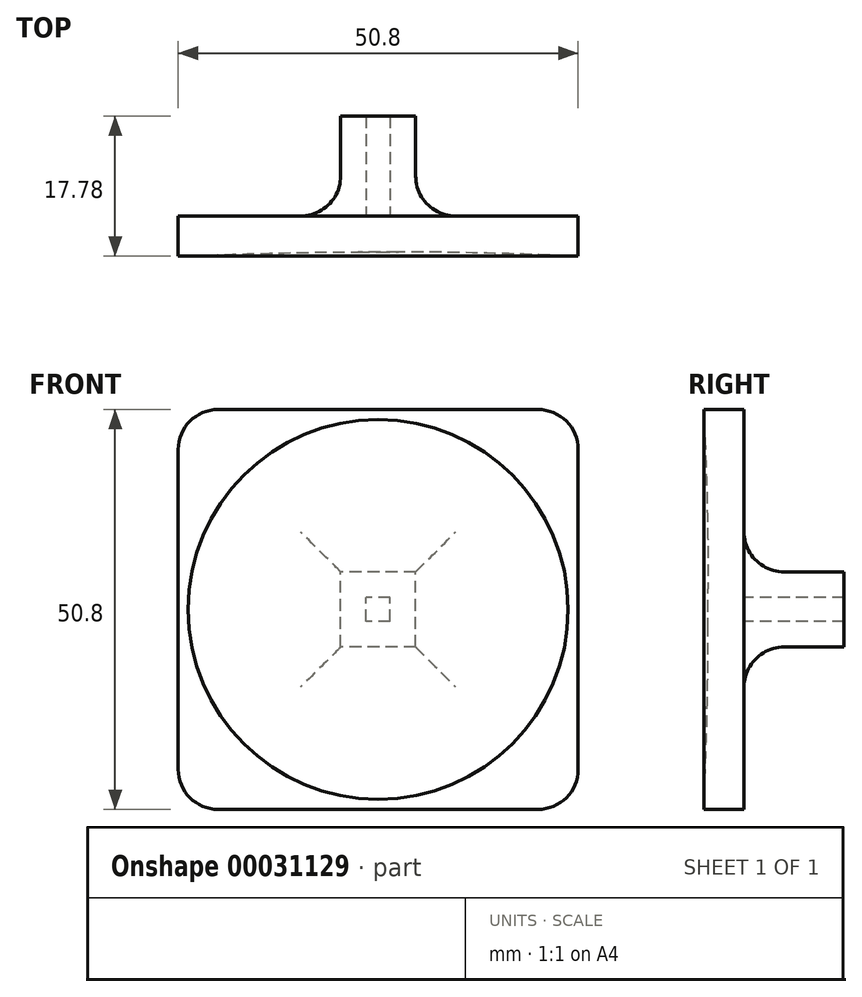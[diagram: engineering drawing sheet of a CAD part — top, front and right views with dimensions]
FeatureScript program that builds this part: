
annotation { "Feature Type Name" : "Feature", "Feature Type Description" : "" }
export const myFeature = defineFeature(function(context is Context, id is Id, definition is map)
    precondition{}
    {
        {
            var Q0;
            Q0=qCreatedBy(makeId("Front.planeOp"),FACE);
            var sketch = newSketch(context, id + "F0", { "sketchPlane" : qUnion([Q0])});
            skLineSegment(sketch, "E0.rect.bottom", {"start": v(25.4, -25.4) * mm, "end": v(-25.4, -25.4) * mm});
            skLineSegment(sketch, "E0.rect.top", {"start": v(25.4, 25.4) * mm, "end": v(-25.4, 25.4) * mm});
            skLineSegment(sketch, "E0.rect.left", {"start": v(25.4, -25.4) * mm, "end": v(25.4, 25.4) * mm});
            skLineSegment(sketch, "E0.rect.right", {"start": v(-25.4, -25.4) * mm, "end": v(-25.4, 25.4) * mm});
            skPoint(sketch, "E0.rect.middle", {"position": v(0, 0) * mm});
            skSolve(sketch);
        }
        {
            var Q0;
            Q0=makeQuery(id+"F0.imprint","IMPRINT",FACE,{"disambiguationData":[TD([[makeQuery(id+"F0.imprint","IMPRINT",EDGE,{"derivedFrom":sQuery(id+"F0.wireOp",EDGE,"E0.rect.bottom")}),-1.0]])]});
            extrude(context, id + "F1", {"entities" : qUnion([Q0]), "depth" : 5.08 * mm});
        }
        {
            var Q0;
            Q0=makeQuery(id+"F1.opExtrude","CAP_FACE",FACE,{"disambiguationData":[OSD([sQuery(id+"F0.wireOp",EDGE,"E0.rect.bottom"),sQuery(id+"F0.wireOp",EDGE,"E0.rect.top"),sQuery(id+"F0.wireOp",EDGE,"E0.rect.left"),sQuery(id+"F0.wireOp",EDGE,"E0.rect.right")])],"isStart":true});
            var sketch = newSketch(context, id + "F2", { "sketchPlane" : qUnion([Q0])});
            skLineSegment(sketch, "E1.rect.bottom", {"start": v(-4.76, -4.76) * mm, "end": v(4.76, -4.76) * mm});
            skLineSegment(sketch, "E1.rect.top", {"start": v(-4.76, 4.76) * mm, "end": v(4.76, 4.76) * mm});
            skLineSegment(sketch, "E1.rect.left", {"start": v(-4.76, -4.76) * mm, "end": v(-4.76, 4.76) * mm});
            skLineSegment(sketch, "E1.rect.right", {"start": v(4.76, -4.76) * mm, "end": v(4.76, 4.76) * mm});
            skPoint(sketch, "E1.rect.middle", {"position": v(0, 0) * mm});
            skLineSegment(sketch, "E2.rect.bottom", {"start": v(-1.52, -1.52) * mm, "end": v(1.52, -1.52) * mm});
            skLineSegment(sketch, "E2.rect.top", {"start": v(-1.52, 1.52) * mm, "end": v(1.52, 1.52) * mm});
            skLineSegment(sketch, "E2.rect.left", {"start": v(-1.52, -1.52) * mm, "end": v(-1.52, 1.52) * mm});
            skLineSegment(sketch, "E2.rect.right", {"start": v(1.52, -1.52) * mm, "end": v(1.52, 1.52) * mm});
            skSolve(sketch);
        }
        {
            var Q0;
            Q0=makeQuery(id+"F2.imprint","IMPRINT",FACE,{"disambiguationData":[TD([[makeQuery(id+"F2.imprint","IMPRINT",EDGE,{"derivedFrom":sQuery(id+"F2.wireOp",EDGE,"E1.rect.bottom")}),1.0]])]});
            extrude(context, id + "F3", {"entities" : qUnion([Q0]), "operationType" : NewBodyOperationType.ADD, "depth" : 12.7 * mm});
        }
        {
            var Q0;
            Q0=makeQuery(id+"F3.opExtrude","CAP_EDGE",EDGE,{"disambiguationData":[OSD([sQuery(id+"F2.wireOp",EDGE,"E1.rect.bottom")])],"isStart":true});
            var Q1;
            Q1=makeQuery(id+"F3.opExtrude","CAP_EDGE",EDGE,{"disambiguationData":[OSD([sQuery(id+"F2.wireOp",EDGE,"E1.rect.right")])],"isStart":true});
            var Q2;
            Q2=makeQuery(id+"F3.opExtrude","CAP_EDGE",EDGE,{"disambiguationData":[OSD([sQuery(id+"F2.wireOp",EDGE,"E1.rect.left")])],"isStart":true});
            var Q3;
            Q3=makeQuery(id+"F3.opExtrude","CAP_EDGE",EDGE,{"disambiguationData":[OSD([sQuery(id+"F2.wireOp",EDGE,"E1.rect.top")])],"isStart":true});
            fillet(context, id + "F4", {"entities" : qUnion([Q0, Q1, Q2, Q3]), "radius" : 5.08 * mm, "tangentPropagation" : true, "allowEdgeOverflow" : false});
        }
        {
            var Q0;
            Q0=makeQuery(id+"F1.opExtrude","SWEPT_EDGE",EDGE,{"disambiguationData":[OSD([sQuery(id+"F0.wireOp",EDGE,"E0.rect.top"),sQuery(id+"F0.wireOp",EDGE,"E0.rect.right")])]});
            var Q1;
            Q1=makeQuery(id+"F1.opExtrude","SWEPT_EDGE",EDGE,{"disambiguationData":[OSD([sQuery(id+"F0.wireOp",EDGE,"E0.rect.bottom"),sQuery(id+"F0.wireOp",EDGE,"E0.rect.right")])]});
            var Q2;
            Q2=makeQuery(id+"F1.opExtrude","SWEPT_EDGE",EDGE,{"disambiguationData":[OSD([sQuery(id+"F0.wireOp",EDGE,"E0.rect.top"),sQuery(id+"F0.wireOp",EDGE,"E0.rect.left")])]});
            var Q3;
            Q3=makeQuery(id+"F1.opExtrude","SWEPT_EDGE",EDGE,{"disambiguationData":[OSD([sQuery(id+"F0.wireOp",EDGE,"E0.rect.bottom"),sQuery(id+"F0.wireOp",EDGE,"E0.rect.left")])]});
            fillet(context, id + "F5", {"entities" : qUnion([Q0, Q1, Q2, Q3]), "radius" : 5.08 * mm, "tangentPropagation" : true, "allowEdgeOverflow" : false});
        }
        {
            var Q0;
            Q0=makeQuery(id+"F1.opExtrude","CAP_FACE",FACE,{"disambiguationData":[OSD([sQuery(id+"F0.wireOp",EDGE,"E0.rect.bottom"),sQuery(id+"F0.wireOp",EDGE,"E0.rect.top"),sQuery(id+"F0.wireOp",EDGE,"E0.rect.left"),sQuery(id+"F0.wireOp",EDGE,"E0.rect.right")])],"isStart":false});
            var sketch = newSketch(context, id + "F6", { "sketchPlane" : qUnion([Q0])});
            skCircle(sketch, "E3", {"center": v(0, 0) * mm, "radius": 24.13 * mm});
            skSolve(sketch);
        }
        {
            var Q0;
            Q0 = qSketchRegion(id + "F6", true);
            extrude(context, id + "F7", {"entities" : qUnion([Q0]), "operationType" : NewBodyOperationType.REMOVE, "oppositeDirection" : true, "depth" : 0.5 * mm});
        }
        {
            var Q0;
            Q0=makeQuery(id+"F7.boolean.opBoolean","COPY",EDGE,{"derivedFrom":makeQuery(id+"F7.opExtrude","CAP_EDGE",EDGE,{"disambiguationData":[OSD([sQuery(id+"F6.wireOp",EDGE,"E3")])],"isStart":false})});
            fillet(context, id + "F8", {"entities" : qUnion([Q0]), "radius" : 457.2 * mm, "tangentPropagation" : true, "allowEdgeOverflow" : false});
        }
    });
